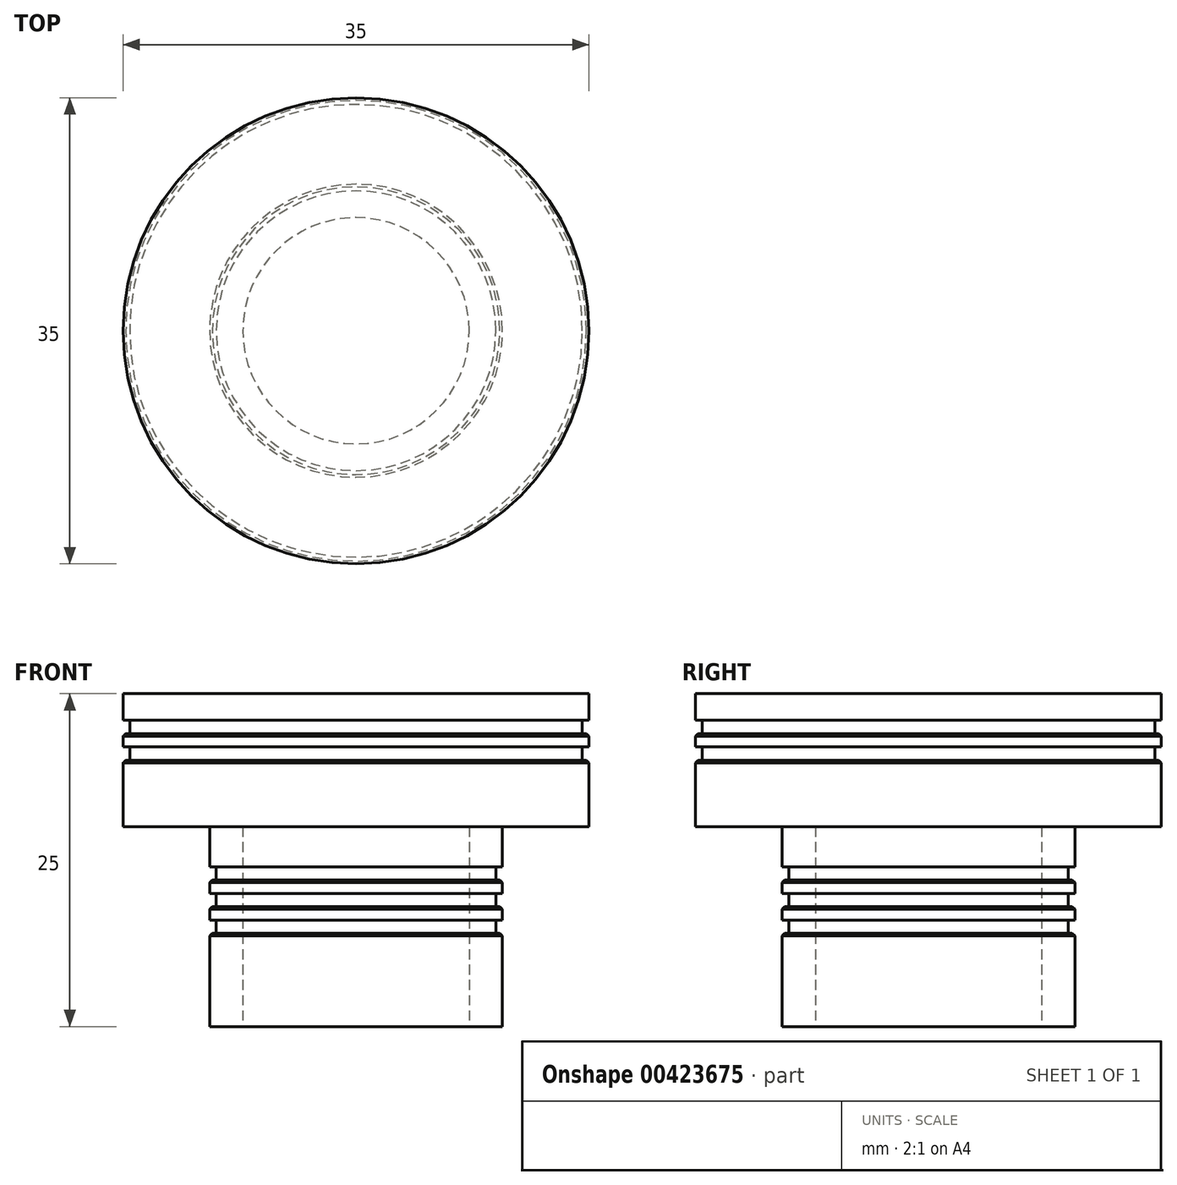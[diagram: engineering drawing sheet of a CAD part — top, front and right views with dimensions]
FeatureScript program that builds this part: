
annotation { "Feature Type Name" : "Feature", "Feature Type Description" : "" }
export const myFeature = defineFeature(function(context is Context, id is Id, definition is map)
    precondition{}
    {
        {
            var Q0;
            Q0=qCreatedBy(makeId("Top.planeOp"),FACE);
            var sketch = newSketch(context, id + "F0", { "sketchPlane" : qUnion([Q0])});
            skCircle(sketch, "E0", {"center": v(0, 0) * mm, "radius": 8.5 * mm});
            skCircle(sketch, "E1", {"center": v(0, 0) * mm, "radius": 11 * mm});
            skSolve(sketch);
        }
        {
            var Q0;
            Q0=makeQuery(id+"F0.imprint","IMPRINT",FACE,{"disambiguationData":[TD([[makeQuery(id+"F0.imprint","IMPRINT",EDGE,{"derivedFrom":sQuery(id+"F0.wireOp",EDGE,"E0")}),-1.0]])]});
            var Q1;
            Q1=sQuery(id+"F0.wireOp",EDGE,"E1");
            var Q2;
            Q2=sQuery(id+"F0.wireOp",EDGE,"E0");
            extrude(context, id + "F1", {"entities" : qUnion([Q0]), "surfaceEntities" : qUnion([Q1, Q2]), "depth" : 15 * mm});
        }
        {
            var Q0;
            Q0=makeQuery(id+"F1.opExtrude","CAP_FACE",FACE,{"disambiguationData":[OSD([sQuery(id+"F0.wireOp",EDGE,"E0"),sQuery(id+"F0.wireOp",EDGE,"E1")])],"isStart":false});
            var sketch = newSketch(context, id + "F2", { "sketchPlane" : qUnion([Q0])});
            skCircle(sketch, "E2", {"center": v(0, 0) * mm, "radius": 17.5 * mm});
            skSolve(sketch);
        }
        {
            var Q0;
            Q0 = qSketchRegion(id + "F2", true);
            extrude(context, id + "F3", {"entities" : qUnion([Q0]), "operationType" : NewBodyOperationType.ADD, "depth" : 10 * mm});
        }
        {
            var Q0;
            Q0=makeQuery(id+"F1.opExtrude","CAP_FACE",FACE,{"disambiguationData":[OSD([sQuery(id+"F0.wireOp",EDGE,"E0"),sQuery(id+"F0.wireOp",EDGE,"E1")])],"isStart":true});
            var sketch = newSketch(context, id + "F4", { "sketchPlane" : qUnion([Q0])});
            skCircle(sketch, "E3", {"center": v(0, 0) * mm, "radius": 11 * mm});
            skCircle(sketch, "E4", {"center": v(0, 0) * mm, "radius": 10.5 * mm});
            skSolve(sketch);
        }
        {
            var Q0;
            Q0 = qSketchRegion(id + "F4", true);
            extrude(context, id + "F5", {"entities" : qUnion([Q0]), "operationType" : NewBodyOperationType.REMOVE, "oppositeDirection" : true, "depth" : 12 * mm});
        }
        {
            var Q0;
            Q0=makeQuery(id+"F1.opExtrude","CAP_FACE",FACE,{"disambiguationData":[OSD([sQuery(id+"F0.wireOp",EDGE,"E0"),sQuery(id+"F0.wireOp",EDGE,"E1")])],"isStart":true});
            var sketch = newSketch(context, id + "F6", { "sketchPlane" : qUnion([Q0])});
            skCircle(sketch, "E5", {"center": v(0, 0) * mm, "radius": 11 * mm});
            skCircle(sketch, "E6", {"center": v(0, 0) * mm, "radius": 10.5 * mm});
            skSolve(sketch);
        }
        {
            var Q0;
            Q0 = qSketchRegion(id + "F6", true);
            extrude(context, id + "F7", {"entities" : qUnion([Q0]), "operationType" : NewBodyOperationType.ADD, "oppositeDirection" : true, "depth" : 11 * mm});
        }
        {
            var Q0;
            Q0=makeQuery(id+"F7.boolean.opBoolean","MERGE",FACE,{"derivedFrom":[makeQuery(id+"F1.opExtrude","CAP_FACE",FACE,{"disambiguationData":[OSD([sQuery(id+"F0.wireOp",EDGE,"E0"),sQuery(id+"F0.wireOp",EDGE,"E1")])],"isStart":true}),makeQuery(id+"F7.opExtrude","CAP_FACE",FACE,{"disambiguationData":[OSD([sQuery(id+"F6.wireOp",EDGE,"E5"),sQuery(id+"F6.wireOp",EDGE,"E6")])],"isStart":true})]});
            var sketch = newSketch(context, id + "F8", { "sketchPlane" : qUnion([Q0])});
            skCircle(sketch, "E7", {"center": v(0, 0) * mm, "radius": 11 * mm});
            skCircle(sketch, "E8", {"center": v(0, 0) * mm, "radius": 10.5 * mm});
            skSolve(sketch);
        }
        {
            var Q0;
            Q0 = qSketchRegion(id + "F8", true);
            extrude(context, id + "F9", {"entities" : qUnion([Q0]), "operationType" : NewBodyOperationType.REMOVE, "oppositeDirection" : true, "depth" : 10 * mm});
        }
        {
            var Q0;
            Q0=makeQuery(id+"F7.boolean.opBoolean","MERGE",FACE,{"derivedFrom":[makeQuery(id+"F1.opExtrude","CAP_FACE",FACE,{"disambiguationData":[OSD([sQuery(id+"F0.wireOp",EDGE,"E0"),sQuery(id+"F0.wireOp",EDGE,"E1")])],"isStart":true}),makeQuery(id+"F7.opExtrude","CAP_FACE",FACE,{"disambiguationData":[OSD([sQuery(id+"F6.wireOp",EDGE,"E5"),sQuery(id+"F6.wireOp",EDGE,"E6")])],"isStart":true})]});
            var sketch = newSketch(context, id + "F10", { "sketchPlane" : qUnion([Q0])});
            skCircle(sketch, "E9", {"center": v(0, 0) * mm, "radius": 11 * mm});
            skCircle(sketch, "E10", {"center": v(0, 0) * mm, "radius": 10.5 * mm});
            skSolve(sketch);
        }
        {
            var Q0;
            Q0 = qSketchRegion(id + "F10", true);
            extrude(context, id + "F11", {"entities" : qUnion([Q0]), "operationType" : NewBodyOperationType.ADD, "oppositeDirection" : true, "depth" : 9 * mm});
        }
        {
            var Q0;
            Q0=makeQuery(id+"F11.boolean.opBoolean","MERGE",FACE,{"derivedFrom":[makeQuery(id+"F7.boolean.opBoolean","MERGE",FACE,{"derivedFrom":[makeQuery(id+"F1.opExtrude","CAP_FACE",FACE,{"disambiguationData":[OSD([sQuery(id+"F0.wireOp",EDGE,"E0"),sQuery(id+"F0.wireOp",EDGE,"E1")])],"isStart":true}),makeQuery(id+"F7.opExtrude","CAP_FACE",FACE,{"disambiguationData":[OSD([sQuery(id+"F6.wireOp",EDGE,"E5"),sQuery(id+"F6.wireOp",EDGE,"E6")])],"isStart":true})]}),makeQuery(id+"F11.opExtrude","CAP_FACE",FACE,{"disambiguationData":[OSD([sQuery(id+"F10.wireOp",EDGE,"E9"),sQuery(id+"F10.wireOp",EDGE,"E10")])],"isStart":true})]});
            var sketch = newSketch(context, id + "F12", { "sketchPlane" : qUnion([Q0])});
            skCircle(sketch, "E11", {"center": v(0, 0) * mm, "radius": 11 * mm});
            skCircle(sketch, "E12", {"center": v(0, 0) * mm, "radius": 10.5 * mm});
            skSolve(sketch);
        }
        {
            var Q0;
            Q0 = qSketchRegion(id + "F12", true);
            extrude(context, id + "F13", {"entities" : qUnion([Q0]), "operationType" : NewBodyOperationType.REMOVE, "oppositeDirection" : true, "depth" : 8 * mm});
        }
        {
            var Q0;
            Q0=makeQuery(id+"F11.boolean.opBoolean","MERGE",FACE,{"derivedFrom":[makeQuery(id+"F7.boolean.opBoolean","MERGE",FACE,{"derivedFrom":[makeQuery(id+"F1.opExtrude","CAP_FACE",FACE,{"disambiguationData":[OSD([sQuery(id+"F0.wireOp",EDGE,"E0"),sQuery(id+"F0.wireOp",EDGE,"E1")])],"isStart":true}),makeQuery(id+"F7.opExtrude","CAP_FACE",FACE,{"disambiguationData":[OSD([sQuery(id+"F6.wireOp",EDGE,"E5"),sQuery(id+"F6.wireOp",EDGE,"E6")])],"isStart":true})]}),makeQuery(id+"F11.opExtrude","CAP_FACE",FACE,{"disambiguationData":[OSD([sQuery(id+"F10.wireOp",EDGE,"E9"),sQuery(id+"F10.wireOp",EDGE,"E10")])],"isStart":true})]});
            var sketch = newSketch(context, id + "F14", { "sketchPlane" : qUnion([Q0])});
            skCircle(sketch, "E13", {"center": v(0, 0) * mm, "radius": 11 * mm});
            skCircle(sketch, "E14", {"center": v(0, 0) * mm, "radius": 10.5 * mm});
            skSolve(sketch);
        }
        {
            var Q0;
            Q0 = qSketchRegion(id + "F14", true);
            extrude(context, id + "F15", {"entities" : qUnion([Q0]), "operationType" : NewBodyOperationType.ADD, "oppositeDirection" : true, "depth" : 7 * mm});
        }
        {
            var Q0;
            {var subQ0=sQuery(id+"F2.wireOp",EDGE,"E2");Q0=makeQuery(id+"F3.boolean.opBoolean","SPLIT",FACE,{"disambiguationData":[TD([makeQuery(id+"F1.opExtrude","SWEPT_FACE",FACE,{"disambiguationData":[OSD([sQuery(id+"F0.wireOp",EDGE,"E1")])]})])],"derivedFrom":makeQuery(id+"F3.opExtrude","CAP_FACE",FACE,{"disambiguationData":[OSD([subQ0])],"isStart":true})});}
            var sketch = newSketch(context, id + "F16", { "sketchPlane" : qUnion([Q0])});
            skCircle(sketch, "E15", {"center": v(0, 0) * mm, "radius": 17.5 * mm});
            skCircle(sketch, "E16", {"center": v(0, 0) * mm, "radius": 17 * mm});
            skSolve(sketch);
        }
        {
            var Q0;
            Q0 = qSketchRegion(id + "F16", true);
            extrude(context, id + "F17", {"entities" : qUnion([Q0]), "operationType" : NewBodyOperationType.REMOVE, "oppositeDirection" : true, "depth" : 8 * mm});
        }
        {
            var Q0;
            {var subQ0=sQuery(id+"F2.wireOp",EDGE,"E2");Q0=makeQuery(id+"F3.boolean.opBoolean","SPLIT",FACE,{"disambiguationData":[TD([makeQuery(id+"F1.opExtrude","SWEPT_FACE",FACE,{"disambiguationData":[OSD([sQuery(id+"F0.wireOp",EDGE,"E1")])]})])],"derivedFrom":makeQuery(id+"F3.opExtrude","CAP_FACE",FACE,{"disambiguationData":[OSD([subQ0])],"isStart":true})});}
            var sketch = newSketch(context, id + "F18", { "sketchPlane" : qUnion([Q0])});
            skCircle(sketch, "E17", {"center": v(0, 0) * mm, "radius": 17.5 * mm});
            skCircle(sketch, "E18", {"center": v(0, 0) * mm, "radius": 17 * mm});
            skSolve(sketch);
        }
        {
            var Q0;
            Q0 = qSketchRegion(id + "F18", true);
            extrude(context, id + "F19", {"entities" : qUnion([Q0]), "operationType" : NewBodyOperationType.ADD, "oppositeDirection" : true, "depth" : 7 * mm});
        }
        {
            var Q0;
            {var subQ0=sQuery(id+"F2.wireOp",EDGE,"E2");Q0=makeQuery(id+"F19.boolean.opBoolean","MERGE",FACE,{"derivedFrom":[makeQuery(id+"F3.boolean.opBoolean","SPLIT",FACE,{"disambiguationData":[TD([makeQuery(id+"F1.opExtrude","SWEPT_FACE",FACE,{"disambiguationData":[OSD([sQuery(id+"F0.wireOp",EDGE,"E1")])]})])],"derivedFrom":makeQuery(id+"F3.opExtrude","CAP_FACE",FACE,{"disambiguationData":[OSD([subQ0])],"isStart":true})}),makeQuery(id+"F19.opExtrude","CAP_FACE",FACE,{"disambiguationData":[OSD([sQuery(id+"F18.wireOp",EDGE,"E17"),sQuery(id+"F18.wireOp",EDGE,"E18")])],"isStart":true})]});}
            var sketch = newSketch(context, id + "F20", { "sketchPlane" : qUnion([Q0])});
            skCircle(sketch, "E19", {"center": v(0, 0) * mm, "radius": 17.5 * mm});
            skCircle(sketch, "E20", {"center": v(0, 0) * mm, "radius": 17 * mm});
            skSolve(sketch);
        }
        {
            var Q0;
            Q0 = qSketchRegion(id + "F20", true);
            extrude(context, id + "F21", {"entities" : qUnion([Q0]), "operationType" : NewBodyOperationType.REMOVE, "oppositeDirection" : true, "depth" : 6 * mm});
        }
        {
            var Q0;
            {var subQ0=sQuery(id+"F2.wireOp",EDGE,"E2");Q0=makeQuery(id+"F19.boolean.opBoolean","MERGE",FACE,{"derivedFrom":[makeQuery(id+"F3.boolean.opBoolean","SPLIT",FACE,{"disambiguationData":[TD([makeQuery(id+"F1.opExtrude","SWEPT_FACE",FACE,{"disambiguationData":[OSD([sQuery(id+"F0.wireOp",EDGE,"E1")])]})])],"derivedFrom":makeQuery(id+"F3.opExtrude","CAP_FACE",FACE,{"disambiguationData":[OSD([subQ0])],"isStart":true})}),makeQuery(id+"F19.opExtrude","CAP_FACE",FACE,{"disambiguationData":[OSD([sQuery(id+"F18.wireOp",EDGE,"E17"),sQuery(id+"F18.wireOp",EDGE,"E18")])],"isStart":true})]});}
            var sketch = newSketch(context, id + "F22", { "sketchPlane" : qUnion([Q0])});
            skCircle(sketch, "E21", {"center": v(0, 0) * mm, "radius": 17.5 * mm});
            skCircle(sketch, "E22", {"center": v(0, 0) * mm, "radius": 17 * mm});
            skSolve(sketch);
        }
        {
            var Q0;
            Q0 = qSketchRegion(id + "F22", true);
            extrude(context, id + "F23", {"entities" : qUnion([Q0]), "operationType" : NewBodyOperationType.ADD, "oppositeDirection" : true, "depth" : 5 * mm});
        }
        {
            var Q0;
            Q0=makeQuery(id+"F17.boolean.opBoolean","COPY",EDGE,{"derivedFrom":makeQuery(id+"F17.opExtrude","CAP_EDGE",EDGE,{"disambiguationData":[OSD([sQuery(id+"F16.wireOp",EDGE,"E15")])],"isStart":false})});
            var Q1;
            Q1=makeQuery(id+"F19.opExtrude","CAP_EDGE",EDGE,{"disambiguationData":[OSD([sQuery(id+"F18.wireOp",EDGE,"E17")])],"isStart":false});
            var Q2;
            Q2=makeQuery(id+"F23.opExtrude","CAP_EDGE",EDGE,{"disambiguationData":[OSD([sQuery(id+"F22.wireOp",EDGE,"E21")])],"isStart":false});
            var Q3;
            Q3=makeQuery(id+"F21.boolean.opBoolean","COPY",EDGE,{"derivedFrom":makeQuery(id+"F21.opExtrude","CAP_EDGE",EDGE,{"disambiguationData":[OSD([sQuery(id+"F20.wireOp",EDGE,"E19")])],"isStart":false})});
            var Q4;
            Q4=makeQuery(id+"F5.boolean.opBoolean","COPY",EDGE,{"derivedFrom":makeQuery(id+"F5.opExtrude","CAP_EDGE",EDGE,{"disambiguationData":[OSD([sQuery(id+"F4.wireOp",EDGE,"E3")])],"isStart":false})});
            var Q5;
            Q5=makeQuery(id+"F9.boolean.opBoolean","COPY",EDGE,{"derivedFrom":makeQuery(id+"F9.opExtrude","CAP_EDGE",EDGE,{"disambiguationData":[OSD([sQuery(id+"F8.wireOp",EDGE,"E7")])],"isStart":false})});
            var Q6;
            Q6=makeQuery(id+"F7.opExtrude","CAP_EDGE",EDGE,{"disambiguationData":[OSD([sQuery(id+"F6.wireOp",EDGE,"E5")])],"isStart":false});
            var Q7;
            Q7=makeQuery(id+"F11.opExtrude","CAP_EDGE",EDGE,{"disambiguationData":[OSD([sQuery(id+"F10.wireOp",EDGE,"E9")])],"isStart":false});
            var Q8;
            Q8=makeQuery(id+"F13.boolean.opBoolean","COPY",EDGE,{"derivedFrom":makeQuery(id+"F13.opExtrude","CAP_EDGE",EDGE,{"disambiguationData":[OSD([sQuery(id+"F12.wireOp",EDGE,"E11")])],"isStart":false})});
            var Q9;
            Q9=makeQuery(id+"F15.opExtrude","CAP_EDGE",EDGE,{"disambiguationData":[OSD([sQuery(id+"F14.wireOp",EDGE,"E13")])],"isStart":false});
            chamfer(context, id + "F24", {"entities" : qUnion([Q0, Q1, Q2, Q3, Q4, Q5, Q6, Q7, Q8, Q9]), "width" : 0.2 * mm, "tangentPropagation" : true});
        }
    });
